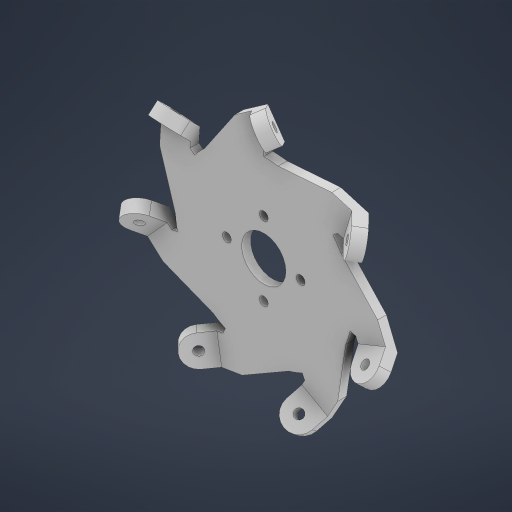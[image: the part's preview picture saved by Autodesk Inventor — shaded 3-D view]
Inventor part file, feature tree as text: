
AUTODESK INVENTOR PART (.ipt)
format: ipt  version: 2023 (Build 270158000, 158)  size: 348,160 bytes
history: native  units: mm
features: extrude x3, sketch x3, pattern_circular x2, plane x1, fillet x1
ambient origin geometry x8: Origin, YZ Plane, XZ Plane, XY Plane, X Axis, Y Axis, Z Axis, Center Point
bodies: Solid1 (feature_tree)
feature tree (10):
  extrude  "Extrusion1"  Depth=2.0mm
  plane  "Work Plane1"
  extrude  "Extrusion2"  Depth=10.0mm
  fillet  "Fillet1"  Radius=10.0mm
  extrude  "Extrusion3"  Depth=3.0mm TaperAngle=360.0deg
  pattern_circular  "Circular Pattern1"  [2 undecoded]
  pattern_circular  "Circular Pattern2"  Angle=135.0deg  [1 undecoded]
  sketch  "Sketch1"  dims[d1=15.0mm d2=2.0mm]
  sketch  "Sketch2"  dims[d4=5.0mm d5=6.108652mm d6=10.0mm]
  sketch  "Sketch3"  dims[d7=10.0mm d8=70.0mm d10=360.0deg d12=3.0mm d13=0.0mm d14=135.0deg d15=10.0mm d16=0.0mm d17=5.0mm d18=3.0mm d19=10.0mm d20=0.0mm d21=70.0mm d22=360.0deg d24=70.0mm d25=360.0deg d28=3.0mm d29=3.0mm d30=3.0mm d31=3.0mm]
note: 3 required parameter values undecoded (feature->parameter linkage not recoverable at this tier; creation-order binding heuristic only, values carry confidence <= 0.55)
